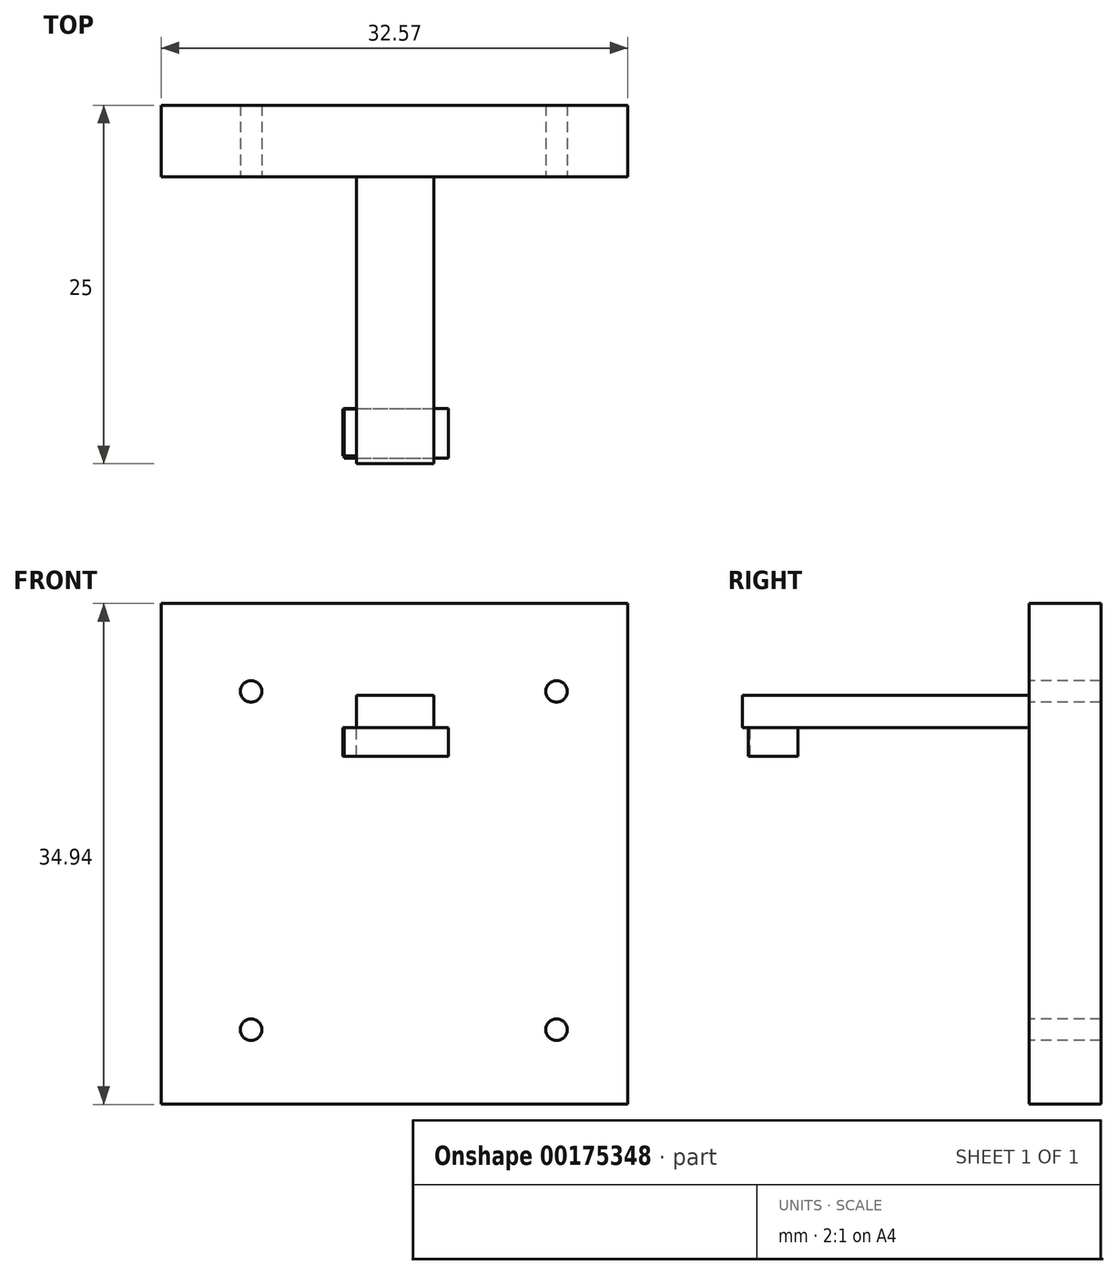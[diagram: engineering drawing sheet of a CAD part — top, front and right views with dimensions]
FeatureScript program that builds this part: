
annotation { "Feature Type Name" : "Feature", "Feature Type Description" : "" }
export const myFeature = defineFeature(function(context is Context, id is Id, definition is map)
    precondition{}
    {
        {
            var Q0;
            Q0=qCreatedBy(makeId("Front.planeOp"),FACE);
            var sketch = newSketch(context, id + "F0", { "sketchPlane" : qUnion([Q0])});
            skLineSegment(sketch, "E0.bottom", {"start": v(-41.45, 29.3) * mm, "end": v(-8.88, 29.3) * mm});
            skLineSegment(sketch, "E0.top", {"start": v(-41.45, -5.63) * mm, "end": v(-8.88, -5.63) * mm});
            skLineSegment(sketch, "E0.left", {"start": v(-41.45, 29.3) * mm, "end": v(-41.45, -5.63) * mm});
            skLineSegment(sketch, "E0.right", {"start": v(-8.88, 29.3) * mm, "end": v(-8.88, -5.63) * mm});
            skSolve(sketch);
        }
        {
            var Q0;
            Q0=makeQuery(id+"F0.imprint","IMPRINT",FACE,{"disambiguationData":[TD([[makeQuery(id+"F0.imprint","IMPRINT",EDGE,{"derivedFrom":sQuery(id+"F0.wireOp",EDGE,"E0.bottom")}),-1.0]])]});
            extrude(context, id + "F1", {"entities" : qUnion([Q0]), "depth" : 5 * mm});
        }
        {
            var Q0;
            Q0=makeQuery(id+"F1.opExtrude","CAP_FACE",FACE,{"disambiguationData":[OSD([sQuery(id+"F0.wireOp",EDGE,"E0.bottom"),sQuery(id+"F0.wireOp",EDGE,"E0.top"),sQuery(id+"F0.wireOp",EDGE,"E0.left"),sQuery(id+"F0.wireOp",EDGE,"E0.right")])],"isStart":true});
            var sketch = newSketch(context, id + "F2", { "sketchPlane" : qUnion([Q0])});
            skLineSegment(sketch, "E1.bottom", {"start": v(22.42, 22.9) * mm, "end": v(27.82, 22.9) * mm});
            skLineSegment(sketch, "E1.top", {"start": v(22.42, 20.66) * mm, "end": v(27.82, 20.66) * mm});
            skLineSegment(sketch, "E1.left", {"start": v(22.42, 22.9) * mm, "end": v(22.42, 20.66) * mm});
            skLineSegment(sketch, "E1.right", {"start": v(27.82, 22.9) * mm, "end": v(27.82, 20.66) * mm});
            skSolve(sketch);
        }
        {
            var Q0;
            Q0 = qSketchRegion(id + "F2", true);
            extrude(context, id + "F3", {"entities" : qUnion([Q0]), "operationType" : NewBodyOperationType.ADD, "oppositeDirection" : true, "depth" : 25 * mm});
        }
        {
            var Q0;
            Q0=makeQuery(id+"F3.opExtrude","SWEPT_FACE",FACE,{"disambiguationData":[OSD([sQuery(id+"F2.wireOp",EDGE,"E1.top")])]});
            var sketch = newSketch(context, id + "F4", { "sketchPlane" : qUnion([Q0])});
            skLineSegment(sketch, "E2.bottom", {"start": v(-28.78, 24.47) * mm, "end": v(-21.56, 24.47) * mm});
            skLineSegment(sketch, "E2.top", {"start": v(-28.78, 21.18) * mm, "end": v(-21.56, 21.18) * mm});
            skLineSegment(sketch, "E2.left", {"start": v(-28.78, 24.47) * mm, "end": v(-28.78, 21.18) * mm});
            skLineSegment(sketch, "E2.right", {"start": v(-21.56, 24.47) * mm, "end": v(-21.56, 21.18) * mm});
            skSolve(sketch);
        }
        {
            var Q0;
            {var subQ0=sQuery(id+"F4.wireOp",EDGE,"E2.left");Q0=makeQuery(id+"F4.imprint","IMPRINT",FACE,{"disambiguationData":[TD([[makeQuery(id+"F4.imprint","IMPRINT",EDGE,{"derivedFrom":subQ0}),1.0]])]});}
            extrude(context, id + "F5", {"entities" : qUnion([Q0]), "depth" : 2 * mm});
        }
        {
            var Q0;
            Q0=makeQuery(id+"F3.opExtrude","SWEPT_FACE",FACE,{"disambiguationData":[OSD([sQuery(id+"F2.wireOp",EDGE,"E1.top")])]});
            var sketch = newSketch(context, id + "F6", { "sketchPlane" : qUnion([Q0])});
            skLineSegment(sketch, "E3.bottom", {"start": v(-28.66, 21.15) * mm, "end": v(-21.39, 21.15) * mm});
            skLineSegment(sketch, "E3.top", {"start": v(-28.66, 24.6) * mm, "end": v(-21.39, 24.6) * mm});
            skLineSegment(sketch, "E3.left", {"start": v(-28.66, 21.15) * mm, "end": v(-28.66, 24.6) * mm});
            skLineSegment(sketch, "E3.right", {"start": v(-21.39, 21.15) * mm, "end": v(-21.39, 24.6) * mm});
            skSolve(sketch);
        }
        {
            var Q0;
            {var subQ0=sQuery(id+"F6.wireOp",EDGE,"E3.left");Q0=makeQuery(id+"F6.imprint","IMPRINT",FACE,{"disambiguationData":[TD([[makeQuery(id+"F6.imprint","IMPRINT",EDGE,{"derivedFrom":subQ0}),-1.0]])]});}
            var Q1;
            {var subQ0=sQuery(id+"F6.wireOp",EDGE,"E3.right");Q1=makeQuery(id+"F6.imprint","IMPRINT",FACE,{"disambiguationData":[TD([[makeQuery(id+"F6.imprint","IMPRINT",EDGE,{"derivedFrom":subQ0}),1.0]])]});}
            var Q2;
            {var subQ0=sQuery(id+"F6.wireOp",EDGE,"E3.bottom");var subQ1=sQuery(id+"F2.wireOp",EDGE,"E1.top");var subQ2=makeQuery(id+"F3.opExtrude","SWEPT_EDGE",EDGE,{"disambiguationData":[OSD([subQ1,sQuery(id+"F2.wireOp",EDGE,"E1.right")])]});var subQ3=makeQuery(id+"F6.imprint","INTERSECT",VERTEX,{"derivedFrom":[subQ2,subQ0]});Q2=makeQuery(id+"F6.imprint","IMPRINT",FACE,{"disambiguationData":[TD([[makeQuery(id+"F6.imprint","IMPRINT",EDGE,{"disambiguationData":[TD([[subQ3,-1.0]])],"derivedFrom":subQ0}),1.0]])]});}
            extrude(context, id + "F7", {"entities" : qUnion([Q0, Q1, Q2]), "depth" : 2 * mm});
        }
        {
            var Q0;
            Q0=makeQuery(id+"F1.opExtrude","CAP_FACE",FACE,{"disambiguationData":[OSD([sQuery(id+"F0.wireOp",EDGE,"E0.bottom"),sQuery(id+"F0.wireOp",EDGE,"E0.top"),sQuery(id+"F0.wireOp",EDGE,"E0.left"),sQuery(id+"F0.wireOp",EDGE,"E0.right")])],"isStart":false});
            var sketch = newSketch(context, id + "F8", { "sketchPlane" : qUnion([Q0])});
            skCircle(sketch, "E4", {"center": v(-35.17, 23.18) * mm, "radius": 1.5 * mm});
            skCircle(sketch, "E5", {"center": v(-13.86, 23.18) * mm, "radius": 1.5 * mm});
            skCircle(sketch, "E6", {"center": v(-35.17, -0.42) * mm, "radius": 1.5 * mm});
            skCircle(sketch, "E7", {"center": v(-13.86, -0.42) * mm, "radius": 1.5 * mm});
            skCircle(sketch, "E8", {"center": v(-35.17, 23.18) * mm, "radius": 0.75 * mm});
            skCircle(sketch, "E9", {"center": v(-13.86, 23.18) * mm, "radius": 0.75 * mm});
            skCircle(sketch, "E10", {"center": v(-35.17, -0.42) * mm, "radius": 0.75 * mm});
            skCircle(sketch, "E11", {"center": v(-13.86, -0.42) * mm, "radius": 0.75 * mm});
            skSolve(sketch);
        }
        {
            var Q0;
            Q0=makeQuery(id+"F8.imprint","IMPRINT",FACE,{"disambiguationData":[TD([[makeQuery(id+"F8.imprint","IMPRINT",EDGE,{"derivedFrom":sQuery(id+"F8.wireOp",EDGE,"E8")}),1.0]])]});
            var Q1;
            Q1=makeQuery(id+"F8.imprint","IMPRINT",FACE,{"disambiguationData":[TD([[makeQuery(id+"F8.imprint","IMPRINT",EDGE,{"derivedFrom":sQuery(id+"F8.wireOp",EDGE,"E9")}),1.0]])]});
            var Q2;
            Q2=makeQuery(id+"F8.imprint","IMPRINT",FACE,{"disambiguationData":[TD([[makeQuery(id+"F8.imprint","IMPRINT",EDGE,{"derivedFrom":sQuery(id+"F8.wireOp",EDGE,"E11")}),1.0]])]});
            var Q3;
            Q3=makeQuery(id+"F8.imprint","IMPRINT",FACE,{"disambiguationData":[TD([[makeQuery(id+"F8.imprint","IMPRINT",EDGE,{"derivedFrom":sQuery(id+"F8.wireOp",EDGE,"E10")}),1.0]])]});
            extrude(context, id + "F9", {"entities" : qUnion([Q0, Q1, Q2, Q3]), "operationType" : NewBodyOperationType.REMOVE, "oppositeDirection" : true, "depth" : 25 * mm});
        }
    });
